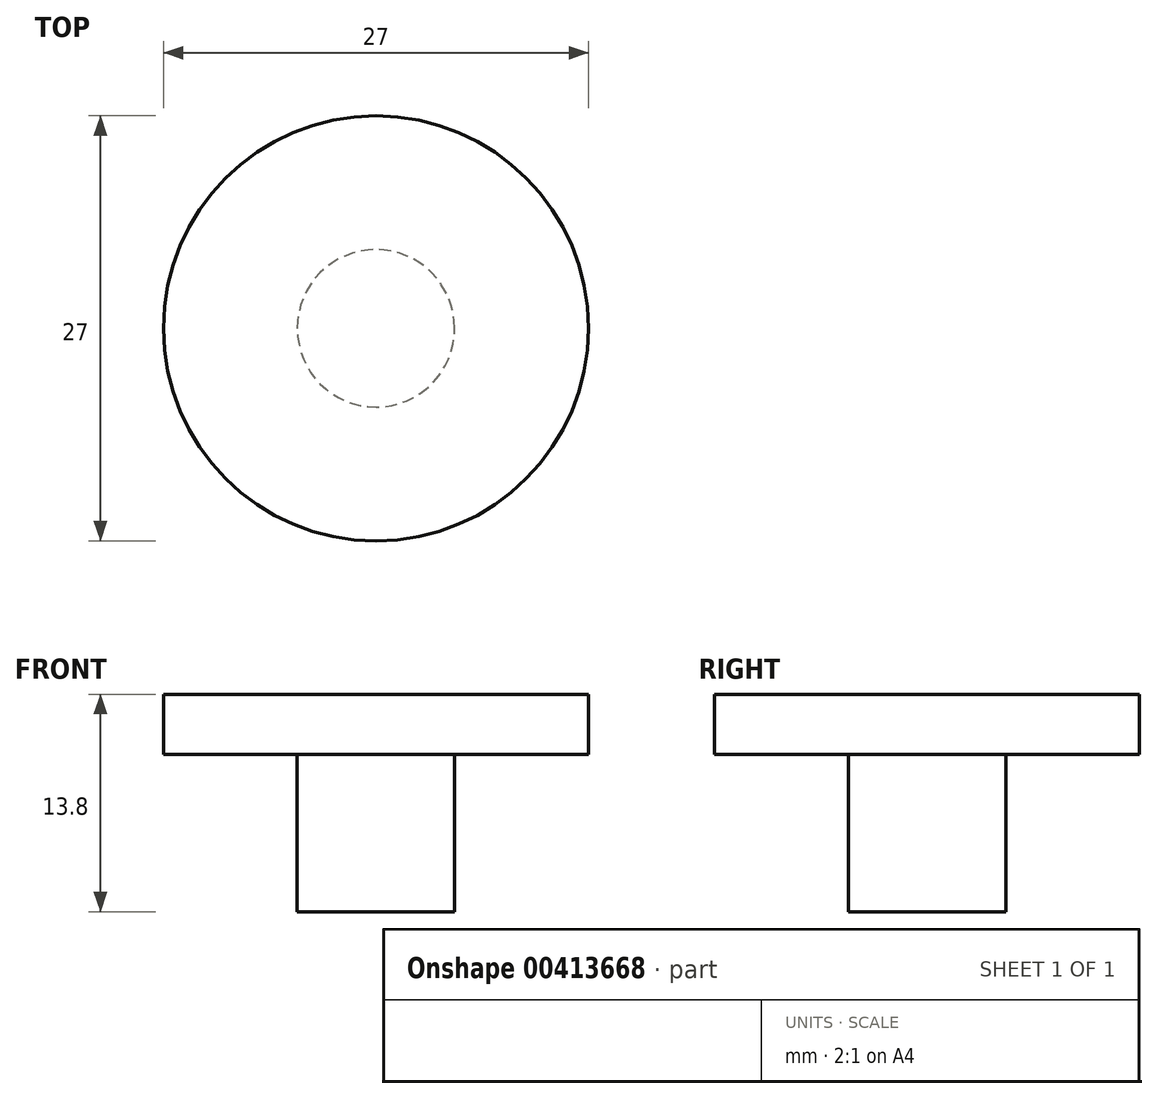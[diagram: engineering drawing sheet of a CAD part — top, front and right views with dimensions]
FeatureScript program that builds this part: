
annotation { "Feature Type Name" : "Feature", "Feature Type Description" : "" }
export const myFeature = defineFeature(function(context is Context, id is Id, definition is map)
    precondition{}
    {
        {
            var Q0;
            Q0=qCreatedBy(makeId("Top.planeOp"),FACE);
            var sketch = newSketch(context, id + "F0", { "sketchPlane" : qUnion([Q0])});
            skCircle(sketch, "E0", {"center": v(0, 0) * mm, "radius": 13.5 * mm});
            skSolve(sketch);
        }
        {
            var Q0;
            Q0=makeQuery(id+"F0.imprint","IMPRINT",FACE,{"disambiguationData":[TD([[makeQuery(id+"F0.imprint","IMPRINT",EDGE,{"derivedFrom":sQuery(id+"F0.wireOp",EDGE,"E0")}),1.0]])]});
            extrude(context, id + "F1", {"entities" : qUnion([Q0]), "depth" : 3.8 * mm, "offsetDistance" : 25 * mm});
        }
        {
            var Q0;
            Q0=makeQuery(id+"F1.opExtrude","CAP_FACE",FACE,{"disambiguationData":[OSD([sQuery(id+"F0.wireOp",EDGE,"E0")])],"isStart":true});
            var sketch = newSketch(context, id + "F2", { "sketchPlane" : qUnion([Q0])});
            skCircle(sketch, "E1", {"center": v(0, 0) * mm, "radius": 5 * mm});
            skSolve(sketch);
        }
        {
            var Q0;
            Q0=makeQuery(id+"F2.imprint","IMPRINT",FACE,{"disambiguationData":[TD([[makeQuery(id+"F2.imprint","IMPRINT",EDGE,{"derivedFrom":sQuery(id+"F2.wireOp",EDGE,"E1")}),1.0]])]});
            var Q1;
            Q1=sQuery(id+"F2.wireOp",EDGE,"E1");
            extrude(context, id + "F3", {"entities" : qUnion([Q0]), "surfaceEntities" : qUnion([Q1]), "depth" : 10 * mm, "offsetDistance" : 25 * mm});
        }
    });
